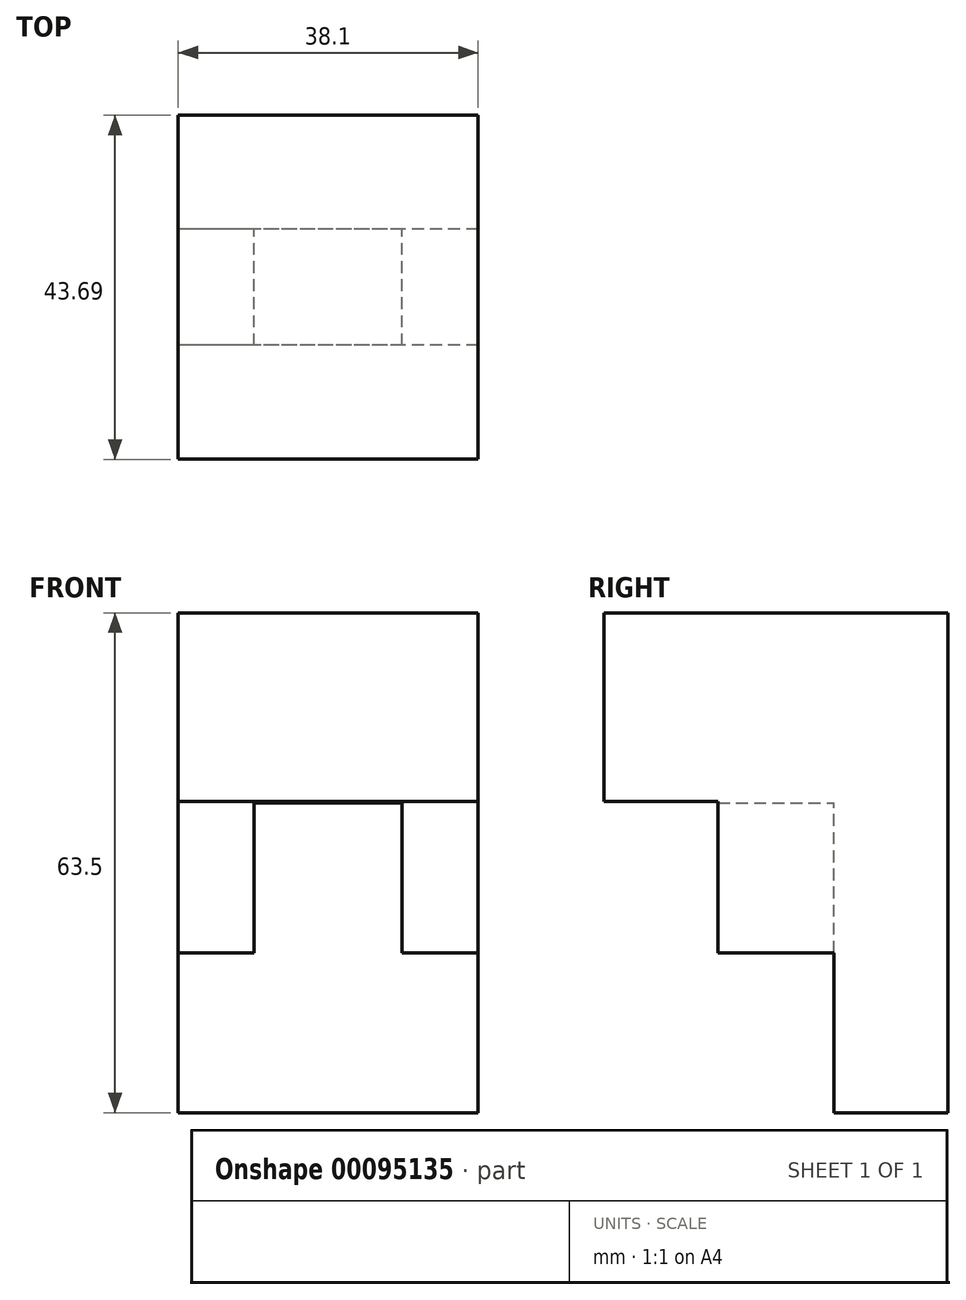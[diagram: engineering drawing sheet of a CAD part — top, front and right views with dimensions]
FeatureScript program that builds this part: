
annotation { "Feature Type Name" : "Feature", "Feature Type Description" : "" }
export const myFeature = defineFeature(function(context is Context, id is Id, definition is map)
    precondition{}
    {
        {
            var Q0;
            Q0=qCreatedBy(makeId("Front.planeOp"),FACE);
            var sketch = newSketch(context, id + "F0", { "sketchPlane" : qUnion([Q0])});
            skLineSegment(sketch, "E0.bottom", {"start": v(-2.89, -5.24) * mm, "end": v(-40.99, -5.24) * mm});
            skLineSegment(sketch, "E0.top", {"start": v(-2.89, 58.26) * mm, "end": v(-40.99, 58.26) * mm});
            skLineSegment(sketch, "E0.left", {"start": v(-2.89, -5.24) * mm, "end": v(-2.89, 58.26) * mm});
            skLineSegment(sketch, "E0.right", {"start": v(-40.99, -5.24) * mm, "end": v(-40.99, 58.26) * mm});
            skPoint(sketch, "E0.middle", {"position": v(-21.94, 26.5) * mm});
            skSolve(sketch);
        }
        {
            var Q0;
            Q0=makeQuery(id+"F0.imprint","IMPRINT",FACE,{"disambiguationData":[TD([[makeQuery(id+"F0.imprint","IMPRINT",EDGE,{"derivedFrom":sQuery(id+"F0.wireOp",EDGE,"E0.bottom")}),-1.0]])]});
            extrude(context, id + "F1", {"entities" : qUnion([Q0]), "depth" : 14.48 * mm});
        }
        {
            var Q0;
            Q0=makeQuery(id+"F1.opExtrude","CAP_FACE",FACE,{"disambiguationData":[OSD([sQuery(id+"F0.wireOp",EDGE,"E0.bottom"),sQuery(id+"F0.wireOp",EDGE,"E0.top"),sQuery(id+"F0.wireOp",EDGE,"E0.left"),sQuery(id+"F0.wireOp",EDGE,"E0.right")])],"isStart":false});
            var sketch = newSketch(context, id + "F2", { "sketchPlane" : qUnion([Q0])});
            skLineSegment(sketch, "E1.bottom", {"start": v(-31.34, 15.08) * mm, "end": v(-40.99, 15.08) * mm});
            skLineSegment(sketch, "E1.top", {"start": v(-31.34, 58.26) * mm, "end": v(-40.99, 58.26) * mm});
            skLineSegment(sketch, "E1.left", {"start": v(-31.34, 15.08) * mm, "end": v(-31.34, 58.26) * mm});
            skLineSegment(sketch, "E1.right", {"start": v(-40.99, 15.08) * mm, "end": v(-40.99, 58.26) * mm});
            skPoint(sketch, "E1.middle", {"position": v(-36.16, 36.67) * mm});
            skLineSegment(sketch, "E2.bottom", {"start": v(-2.89, 15.08) * mm, "end": v(-12.54, 15.08) * mm});
            skLineSegment(sketch, "E2.top", {"start": v(-2.89, 58.26) * mm, "end": v(-12.54, 58.26) * mm});
            skLineSegment(sketch, "E2.left", {"start": v(-2.89, 15.08) * mm, "end": v(-2.89, 58.26) * mm});
            skLineSegment(sketch, "E2.right", {"start": v(-12.54, 15.08) * mm, "end": v(-12.54, 58.26) * mm});
            skPoint(sketch, "E2.middle", {"position": v(-7.71, 36.67) * mm});
            skSolve(sketch);
        }
        {
            var Q0;
            Q0=makeQuery(id+"F2.imprint","IMPRINT",FACE,{"disambiguationData":[TD([[makeQuery(id+"F2.imprint","IMPRINT",EDGE,{"derivedFrom":sQuery(id+"F2.wireOp",EDGE,"E1.bottom")}),-1.0]])]});
            var Q1;
            Q1=makeQuery(id+"F2.imprint","IMPRINT",FACE,{"disambiguationData":[TD([[makeQuery(id+"F2.imprint","IMPRINT",EDGE,{"derivedFrom":sQuery(id+"F2.wireOp",EDGE,"E2.bottom")}),-1.0]])]});
            extrude(context, id + "F3", {"entities" : qUnion([Q0, Q1]), "operationType" : NewBodyOperationType.ADD, "depth" : 14.73 * mm});
        }
        {
            var Q0;
            {var subQ6=sQuery(id+"F2.wireOp",EDGE,"E1.bottom");Q0=makeQuery(id+"F2.imprint","IMPRINT",FACE,{"disambiguationData":[TD([[makeQuery(id+"F2.imprint","IMPRINT",EDGE,{"derivedFrom":subQ6}),1.0]])]});}
            var sketch = newSketch(context, id + "F4", { "sketchPlane" : qUnion([Q0])});
            skLineSegment(sketch, "E3.bottom", {"start": v(-12.54, 34.13) * mm, "end": v(-31.34, 34.13) * mm});
            skLineSegment(sketch, "E3.top", {"start": v(-12.54, 58.26) * mm, "end": v(-31.34, 58.26) * mm});
            skLineSegment(sketch, "E3.left", {"start": v(-12.54, 34.13) * mm, "end": v(-12.54, 58.26) * mm});
            skLineSegment(sketch, "E3.right", {"start": v(-31.34, 34.13) * mm, "end": v(-31.34, 58.26) * mm});
            skPoint(sketch, "E3.middle", {"position": v(-21.94, 46.2) * mm});
            skSolve(sketch);
        }
        {
            var Q0;
            Q0=makeQuery(id+"F4.imprint","IMPRINT",FACE,{"disambiguationData":[TD([[makeQuery(id+"F4.imprint","IMPRINT",EDGE,{"derivedFrom":sQuery(id+"F4.wireOp",EDGE,"E3.bottom")}),-1.0]])]});
            var Q1;
            Q1=makeQuery(id+"F3.opExtrude","CAP_FACE",FACE,{"disambiguationData":[OSD([sQuery(id+"F2.wireOp",EDGE,"E1.bottom"),sQuery(id+"F2.wireOp",EDGE,"E1.top"),sQuery(id+"F2.wireOp",EDGE,"E1.left"),sQuery(id+"F2.wireOp",EDGE,"E1.right")])],"isStart":false});
            extrude(context, id + "F5", {"entities" : qUnion([Q0]), "operationType" : NewBodyOperationType.ADD, "endBound" : BoundingType.UP_TO_SURFACE, "endBoundEntityFace" : qUnion([Q1]), "depth" : 25.4 * mm});
        }
        {
            var Q0;
            Q0=makeQuery(id+"F5.boolean.opBoolean","MERGE",FACE,{"derivedFrom":[makeQuery(id+"F3.opExtrude","CAP_FACE",FACE,{"disambiguationData":[OSD([sQuery(id+"F2.wireOp",EDGE,"E1.bottom"),sQuery(id+"F2.wireOp",EDGE,"E1.top"),sQuery(id+"F2.wireOp",EDGE,"E1.left"),sQuery(id+"F2.wireOp",EDGE,"E1.right")])],"isStart":false}),makeQuery(id+"F3.opExtrude","CAP_FACE",FACE,{"disambiguationData":[OSD([sQuery(id+"F2.wireOp",EDGE,"E2.bottom"),sQuery(id+"F2.wireOp",EDGE,"E2.top"),sQuery(id+"F2.wireOp",EDGE,"E2.left"),sQuery(id+"F2.wireOp",EDGE,"E2.right")])],"isStart":false}),makeQuery(id+"F5.opExtrude","CAP_FACE",FACE,{"disambiguationData":[OSD([sQuery(id+"F4.wireOp",EDGE,"E3.bottom"),sQuery(id+"F4.wireOp",EDGE,"E3.top"),sQuery(id+"F4.wireOp",EDGE,"E3.left"),sQuery(id+"F4.wireOp",EDGE,"E3.right")])],"isStart":false})]});
            var sketch = newSketch(context, id + "F6", { "sketchPlane" : qUnion([Q0])});
            skLineSegment(sketch, "E4.bottom", {"start": v(-2.89, 34.3) * mm, "end": v(-40.99, 34.3) * mm});
            skLineSegment(sketch, "E4.top", {"start": v(-2.89, 58.26) * mm, "end": v(-40.99, 58.26) * mm});
            skLineSegment(sketch, "E4.left", {"start": v(-2.89, 34.3) * mm, "end": v(-2.89, 58.26) * mm});
            skLineSegment(sketch, "E4.right", {"start": v(-40.99, 34.3) * mm, "end": v(-40.99, 58.26) * mm});
            skPoint(sketch, "E4.middle", {"position": v(-21.94, 46.28) * mm});
            skSolve(sketch);
        }
        {
            var Q0;
            Q0=makeQuery(id+"F6.imprint","IMPRINT",FACE,{"disambiguationData":[TD([[makeQuery(id+"F6.imprint","IMPRINT",EDGE,{"derivedFrom":sQuery(id+"F6.wireOp",EDGE,"E4.bottom")}),-1.0]])]});
            extrude(context, id + "F7", {"entities" : qUnion([Q0]), "operationType" : NewBodyOperationType.ADD, "depth" : 14.48 * mm});
        }
    });
